# Revit family: Deckel mit Drehriegel_für Kabelrinne und Kabelleiter_NB75-NB900
name_source: partatom
category: Allgemeines Modell
revit_build: Autodesk Revit 2015 (Build: 20140606_1530(x64)
units: mm (PartAtom-declared; Revit-internal decimal feet)

## types (31) — shared parameters
Height = 13 mm
Hersteller = OBO Bettermann
Length = 3000 mm  [stored 9.84252 ft]
Length 1 = 200 mm  [stored 0.656168 ft]
Length 2 = 1500 mm  [stored 4.92126 ft]
URL = http://www.obo-bettermann.com

## per-type parameters (varying)
| type | GTIN | Manufacturer Art.No. | Material | Width | Width 1 | Width 2 |
| DRL 075 FS | 4012196385577 | 6052029 | Strip galvanised | 77 mm  [stored 0.252625 ft] | 1 mm  [stored 0.00328084 ft] | 25 mm  [stored 0.082021 ft] |
| DRL 100 FS | 4012196057979 | 6052096 | Strip galvanised | 102 mm | 1 mm  [stored 0.00328084 ft] | 26 mm |
| DRL 100 DD | 4012196038770 | 6052703 | Strip galvanised zinc/aluminium | 102 mm | 1 mm  [stored 0.00328084 ft] | 26 mm |
| DRL 100 FT | 4012196432370 | 6051340 | Hot-dip galvanised | 102 mm | 1 mm  [stored 0.00328084 ft] | 26 mm |
| DRL 1,5 100 FT | 4012196190508 | 6051345 | Hot-dip galvanised | 102 mm | 2 mm  [stored 0.00656168 ft] | 26 mm |
| DRL 150 FS | 4012196058099 | 6052150 | Strip galvanised | 152 mm  [stored 0.498688 ft] | 1 mm  [stored 0.00328084 ft] | 26 mm |
| DRL 150 DD | 4012196038831 | 6052706 | Strip galvanised zinc/aluminium | 152 mm  [stored 0.498688 ft] | 1 mm  [stored 0.00328084 ft] | 26 mm |
| DRL 150 FT | 4012196432257 | 6051359 | Hot-dip galvanised | 152 mm  [stored 0.498688 ft] | 1 mm  [stored 0.00328084 ft] | 26 mm |
| DRL 200 FS | 4012196058150 | 6052207 | Strip galvanised | 202 mm  [stored 0.66273 ft] | 1 mm  [stored 0.00328084 ft] | 26 mm |
| DRL 200 DD | 4012196038893 | 6052709 | Strip galvanised zinc/aluminium | 202 mm  [stored 0.66273 ft] | 1 mm  [stored 0.00328084 ft] | 26 mm |
| DRL 200 FT | 4012196611898 | 6051367 | Hot-dip galvanised | 202 mm  [stored 0.66273 ft] | 1 mm  [stored 0.00328084 ft] | 26 mm |
| DRL 300 FS | 4012196058273 | 6052304 | Strip galvanised | 302 mm  [stored 0.990814 ft] | 1 mm  [stored 0.00328084 ft] | 26 mm |
| DRL 300 DD | 4012196038954 | 6052712 | Strip galvanised zinc/aluminium | 302 mm  [stored 0.990814 ft] | 1 mm  [stored 0.00328084 ft] | 26 mm |
| DRL 300 FT | 4012196611775 | 6051383 | Hot-dip galvanised | 302 mm  [stored 0.990814 ft] | 1 mm  [stored 0.00328084 ft] | 26 mm |
| DRL 300 FT SO | 4012195624103 | 7196037 | Hot-dip galvanised | 302 mm  [stored 0.990814 ft] | 1 mm  [stored 0.00328084 ft] | 26 mm |
| DRL 400 FS | 4012196058396 | 6052401 | Strip galvanised | 402 mm  [stored 1.3189 ft] | 1 mm  [stored 0.00328084 ft] | 26 mm |
| DRL 400 DD | 4012196039012 | 6052715 | Strip galvanised zinc/aluminium | 402 mm  [stored 1.3189 ft] | 1 mm  [stored 0.00328084 ft] | 26 mm |
| DRL 400 FT | 4012196611713 | 6051413 | Hot-dip galvanised | 402 mm  [stored 1.3189 ft] | 2 mm  [stored 0.00656168 ft] | 26 mm |
| DRL 450 FT | 4012195460145 | 6052450 | Hot-dip galvanised | 452 mm  [stored 1.48294 ft] | 2 mm  [stored 0.00656168 ft] | 27 mm |
| DRL 500 FS | 4012196058518 | 6052509 | Strip galvanised | 502 mm  [stored 1.64698 ft] | 2 mm  [stored 0.00656168 ft] | 27 mm |
| DRL 500 DD | 4012196039074 | 6052718 | Strip galvanised zinc/aluminium | 502 mm  [stored 1.64698 ft] | 2 mm  [stored 0.00656168 ft] | 27 mm |
| DRL 500 FT | 4012196087792 | 6051448 | Hot-dip galvanised | 502 mm  [stored 1.64698 ft] | 2 mm  [stored 0.00656168 ft] | 27 mm |
| DRL 500 FT SO | 4012195652427 | 7196045 | Hot-dip galvanised | 502 mm  [stored 1.64698 ft] | 2 mm  [stored 0.00656168 ft] | 27 mm |
| DRL 550 FS | 4012196058631 | 6052568 | Strip galvanised | 552 mm  [stored 1.81102 ft] | 2 mm  [stored 0.00656168 ft] | 27 mm |
| DRL 550 DD | 4012196039135 | 6052721 | Strip galvanised zinc/aluminium | 552 mm  [stored 1.81102 ft] | 2 mm  [stored 0.00656168 ft] | 27 mm |
| DRL 600 FS | 4012196058754 | 6052606 | Strip galvanised | 602 mm  [stored 1.97507 ft] | 2 mm  [stored 0.00656168 ft] | 27 mm |
| DRL 600 DD | 4012196039197 | 6052724 | Strip galvanised zinc/aluminium | 602 mm  [stored 1.97507 ft] | 2 mm  [stored 0.00656168 ft] | 27 mm |
| DRL 600 FT | 4012196595631 | 6051472 | Hot-dip galvanised | 602 mm  [stored 1.97507 ft] | 2 mm  [stored 0.00656168 ft] | 27 mm |
| DRL 600 FT SO | 4012195624127 | 7196061 | Hot-dip galvanised | 602 mm  [stored 1.97507 ft] | 2 mm  [stored 0.00656168 ft] | 27 mm |
| DRL 750 DD | 4012196127894 | 6052725 | Strip galvanised zinc/aluminium | 752 mm  [stored 2.46719 ft] | 2 mm  [stored 0.00656168 ft] | 28 mm |
| DRL 900 FT | 4012196190553 | 6051481 | Hot-dip galvanised | 902 mm  [stored 2.95932 ft] | 2 mm  [stored 0.00656168 ft] | 28 mm |

note: column(s) folded — value = type name in every type: Article Type

note: [stored X ft] marks values corroborated as IEEE doubles in the binary element streams (Revit-internal decimal feet)

## geometry (parser evidence)
native form markers: Sweep x3
no freeform markers — native parametric forms only
